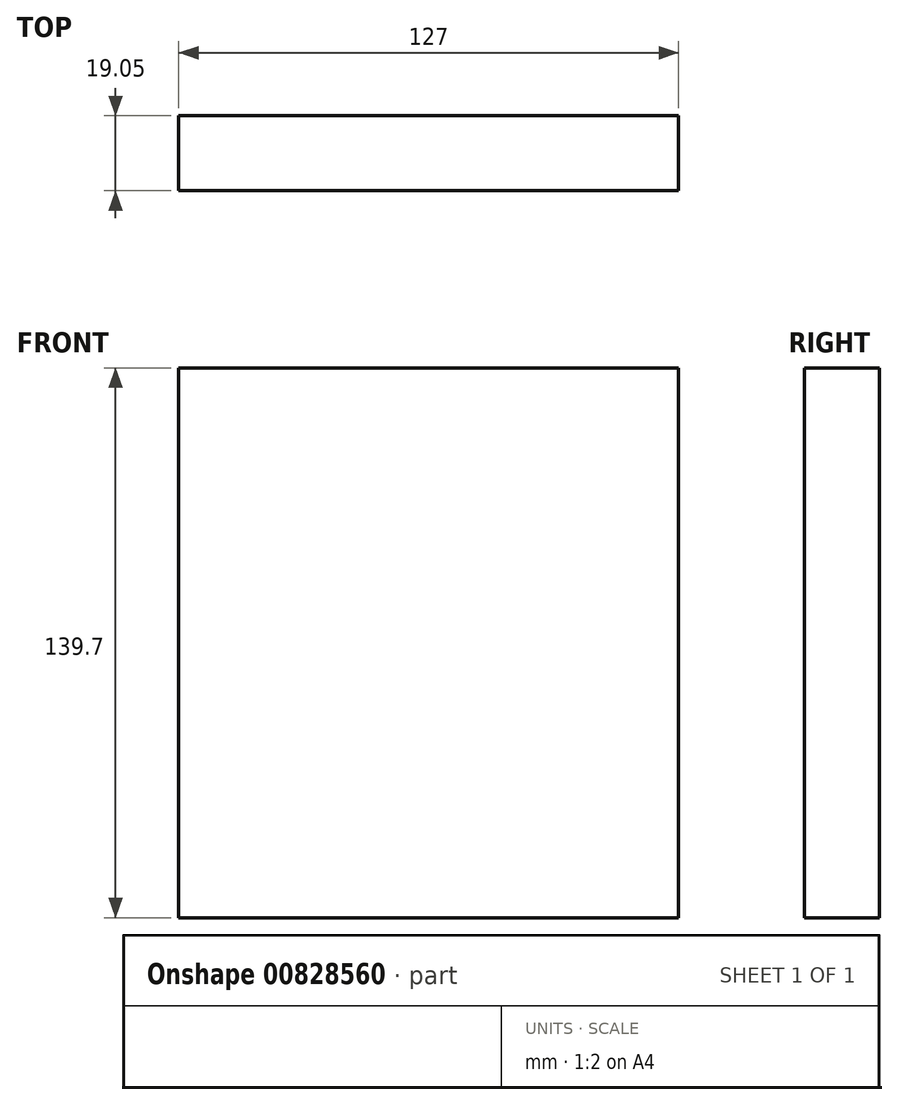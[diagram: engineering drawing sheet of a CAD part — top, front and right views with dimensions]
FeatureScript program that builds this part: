
annotation { "Feature Type Name" : "Feature", "Feature Type Description" : "" }
export const myFeature = defineFeature(function(context is Context, id is Id, definition is map)
    precondition{}
    {
        {
            var Q0;
            Q0=qCreatedBy(makeId("Front.planeOp"),FACE);
            var sketch = newSketch(context, id + "F0", { "sketchPlane" : qUnion([Q0])});
            skLineSegment(sketch, "E0.bottom", {"start": v(0, 0) * mm, "end": v(127, 0) * mm});
            skLineSegment(sketch, "E0.top", {"start": v(0, 139.7) * mm, "end": v(127, 139.7) * mm});
            skLineSegment(sketch, "E0.left", {"start": v(0, 0) * mm, "end": v(0, 139.7) * mm});
            skLineSegment(sketch, "E0.right", {"start": v(127, 0) * mm, "end": v(127, 139.7) * mm});
            skSolve(sketch);
        }
        {
            var Q0;
            Q0 = qSketchRegion(id + "F0", true);
            extrude(context, id + "F1", {"entities" : qUnion([Q0]), "depth" : 19.05 * mm, "offsetDistance" : 25.4 * mm});
        }
    });
